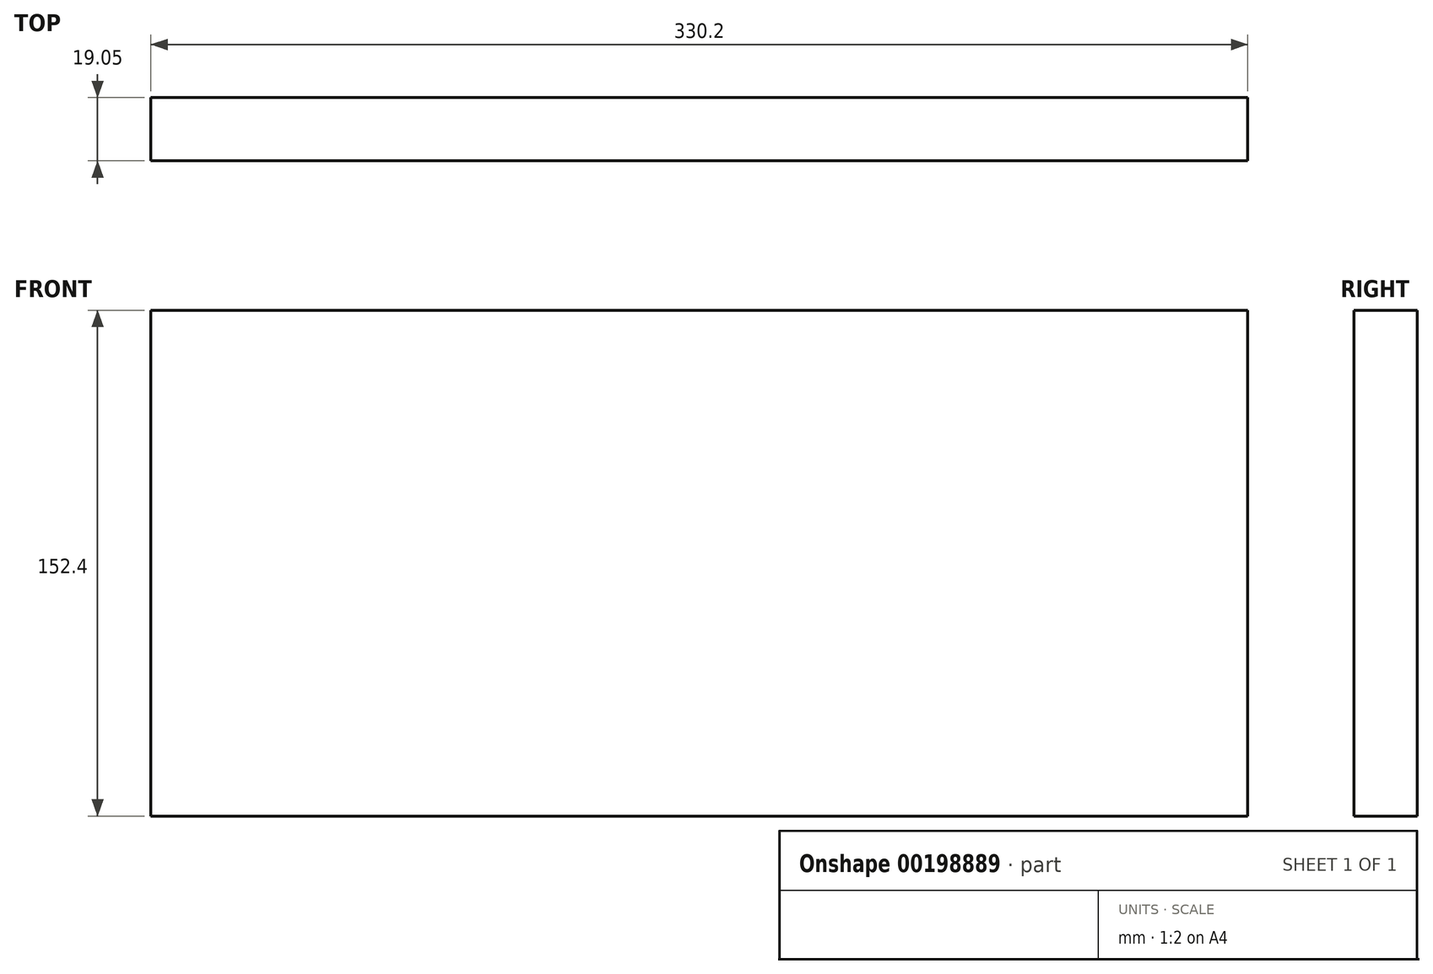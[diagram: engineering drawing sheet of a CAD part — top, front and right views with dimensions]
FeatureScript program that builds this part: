
annotation { "Feature Type Name" : "Feature", "Feature Type Description" : "" }
export const myFeature = defineFeature(function(context is Context, id is Id, definition is map)
    precondition{}
    {
        {
            var Q0;
            Q0=qCreatedBy(makeId("Front.planeOp"),FACE);
            var sketch = newSketch(context, id + "F0", { "sketchPlane" : qUnion([Q0])});
            skLineSegment(sketch, "E0.bottom", {"start": v(0, 0) * mm, "end": v(304.8, 0) * mm});
            skLineSegment(sketch, "E0.top", {"start": v(0, 152.4) * mm, "end": v(304.8, 152.4) * mm});
            skLineSegment(sketch, "E0.left", {"start": v(0, 0) * mm, "end": v(0, 152.4) * mm});
            skLineSegment(sketch, "E0.right", {"start": v(304.8, 0) * mm, "end": v(304.8, 152.4) * mm});
            skSolve(sketch);
        }
        {
            var Q0;
            Q0=makeQuery(id+"F0.imprint","IMPRINT",FACE,{"disambiguationData":[TD([[makeQuery(id+"F0.imprint","IMPRINT",EDGE,{"derivedFrom":sQuery(id+"F0.wireOp",EDGE,"E0.bottom")}),1.0]])]});
            extrude(context, id + "F1", {"entities" : qUnion([Q0]), "oppositeDirection" : true, "depth" : 19.05 * mm});
        }
        {
            var Q0;
            Q0=makeQuery(id+"F1.opExtrude","SWEPT_FACE",FACE,{"disambiguationData":[OSD([sQuery(id+"F0.wireOp",EDGE,"E0.right")])]});
            var sketch = newSketch(context, id + "F2", { "sketchPlane" : qUnion([Q0])});
            skLineSegment(sketch, "E1.bottom", {"start": v(0, 152.4) * mm, "end": v(19.05, 152.4) * mm});
            skLineSegment(sketch, "E1.top", {"start": v(0, 127) * mm, "end": v(19.05, 127) * mm});
            skLineSegment(sketch, "E1.left", {"start": v(0, 152.4) * mm, "end": v(0, 127) * mm});
            skLineSegment(sketch, "E1.right", {"start": v(19.05, 152.4) * mm, "end": v(19.05, 127) * mm});
            skLineSegment(sketch, "E2.bottom", {"start": v(19.05, 0) * mm, "end": v(0, 0) * mm});
            skLineSegment(sketch, "E2.top", {"start": v(19.05, 25.4) * mm, "end": v(0, 25.4) * mm});
            skLineSegment(sketch, "E2.left", {"start": v(19.05, 0) * mm, "end": v(19.05, 25.4) * mm});
            skLineSegment(sketch, "E2.right", {"start": v(0, 0) * mm, "end": v(0, 25.4) * mm});
            skLineSegment(sketch, "E3.top", {"start": v(19.05, 50.8) * mm, "end": v(0, 50.8) * mm});
            skLineSegment(sketch, "E3.left", {"start": v(19.05, 25.4) * mm, "end": v(19.05, 50.8) * mm});
            skLineSegment(sketch, "E3.right", {"start": v(0, 25.4) * mm, "end": v(0, 50.8) * mm});
            skLineSegment(sketch, "E4.top", {"start": v(19.05, 76.2) * mm, "end": v(0, 76.2) * mm});
            skLineSegment(sketch, "E4.left", {"start": v(19.05, 50.8) * mm, "end": v(19.05, 76.2) * mm});
            skLineSegment(sketch, "E4.right", {"start": v(0, 50.8) * mm, "end": v(0, 76.2) * mm});
            skLineSegment(sketch, "E5.bottom", {"start": v(0, 76.2) * mm, "end": v(19.05, 76.2) * mm});
            skLineSegment(sketch, "E5.top", {"start": v(0, 101.6) * mm, "end": v(19.05, 101.6) * mm});
            skLineSegment(sketch, "E5.left", {"start": v(0, 76.2) * mm, "end": v(0, 101.6) * mm});
            skLineSegment(sketch, "E5.right", {"start": v(19.05, 76.2) * mm, "end": v(19.05, 101.6) * mm});
            skLineSegment(sketch, "E6.left", {"start": v(0, 127) * mm, "end": v(0, 101.6) * mm});
            skLineSegment(sketch, "E6.right", {"start": v(19.05, 127) * mm, "end": v(19.05, 101.6) * mm});
            skSolve(sketch);
        }
        {
            var Q0;
            Q0 = qSketchRegion(id + "F2", true);
            extrude(context, id + "F3", {"entities" : qUnion([Q0]), "operationType" : NewBodyOperationType.ADD, "depth" : 25.4 * mm});
        }
    });
